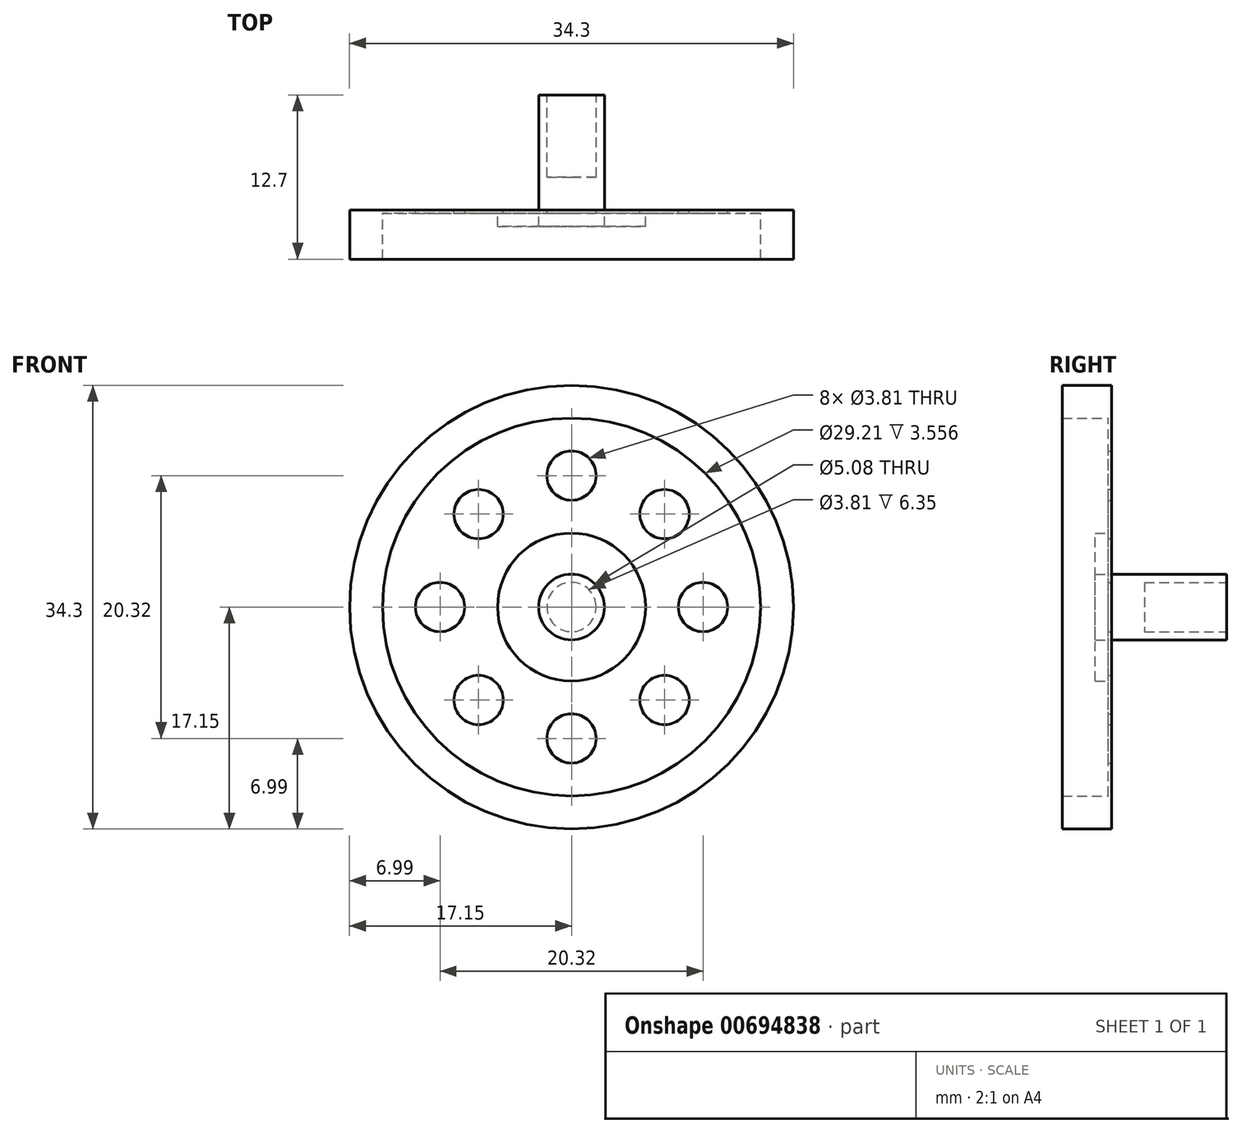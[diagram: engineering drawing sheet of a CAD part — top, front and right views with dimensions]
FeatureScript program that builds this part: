
annotation { "Feature Type Name" : "Feature", "Feature Type Description" : "" }
export const myFeature = defineFeature(function(context is Context, id is Id, definition is map)
    precondition{}
    {
        {
            var Q0;
            Q0=qCreatedBy(makeId("Front.planeOp"),FACE);
            var sketch = newSketch(context, id + "F0", { "sketchPlane" : qUnion([Q0])});
            skCircle(sketch, "E0", {"center": v(0, 0) * mm, "radius": 17.15 * mm});
            skCircle(sketch, "E1.0", {"center": v(0, 0) * mm, "radius": 14.6 * mm});
            skCircle(sketch, "E2", {"center": v(0, 0) * mm, "radius": 2.54 * mm});
            skCircle(sketch, "E3", {"center": v(0, 0) * mm, "radius": 5.72 * mm});
            skCircle(sketch, "E4", {"center": v(0, 10.16) * mm, "radius": 1.9 * mm});
            skCircle(sketch, "E5.1.0", {"center": v(-7.18, 7.18) * mm, "radius": 1.9 * mm});
            skCircle(sketch, "E5.2.0", {"center": v(-10.16, 0) * mm, "radius": 1.9 * mm});
            skCircle(sketch, "E5.3.0", {"center": v(-7.18, -7.18) * mm, "radius": 1.9 * mm});
            skCircle(sketch, "E5.4.0", {"center": v(0, -10.16) * mm, "radius": 1.9 * mm});
            skCircle(sketch, "E5.5.0", {"center": v(7.18, -7.18) * mm, "radius": 1.9 * mm});
            skCircle(sketch, "E5.6.0", {"center": v(10.16, 0) * mm, "radius": 1.9 * mm});
            skCircle(sketch, "E5.7.0", {"center": v(7.18, 7.18) * mm, "radius": 1.9 * mm});
            skSolve(sketch);
        }
        {
            var Q0;
            Q0=makeQuery(id+"F0.imprint","IMPRINT",FACE,{"disambiguationData":[TD([[makeQuery(id+"F0.imprint","IMPRINT",EDGE,{"derivedFrom":sQuery(id+"F0.wireOp",EDGE,"E0")}),1.0]])]});
            extrude(context, id + "F1", {"entities" : qUnion([Q0]), "depth" : 3.8 * mm, "offsetDistance" : 25.4 * mm});
        }
        {
            var Q0;
            Q0=makeQuery(id+"F0.imprint","IMPRINT",FACE,{"disambiguationData":[TD([[makeQuery(id+"F0.imprint","IMPRINT",EDGE,{"derivedFrom":sQuery(id+"F0.wireOp",EDGE,"E2")}),-1.0]])]});
            extrude(context, id + "F2", {"entities" : qUnion([Q0]), "operationType" : NewBodyOperationType.ADD, "depth" : 1.27 * mm, "offsetDistance" : 25.4 * mm});
        }
        {
            var Q0;
            Q0=makeQuery(id+"F0.imprint","IMPRINT",FACE,{"disambiguationData":[TD([[makeQuery(id+"F0.imprint","IMPRINT",EDGE,{"derivedFrom":sQuery(id+"F0.wireOp",EDGE,"E3")}),-1.0]])]});
            extrude(context, id + "F3", {"entities" : qUnion([Q0]), "operationType" : NewBodyOperationType.ADD, "depth" : 0.25 * mm, "offsetDistance" : 25.4 * mm});
        }
        {
            var Q0;
            Q0=makeQuery(id+"F0.imprint","IMPRINT",FACE,{"disambiguationData":[TD([[makeQuery(id+"F0.imprint","IMPRINT",EDGE,{"derivedFrom":sQuery(id+"F0.wireOp",EDGE,"E2")}),1.0]])]});
            extrude(context, id + "F4", {"entities" : qUnion([Q0]), "operationType" : NewBodyOperationType.ADD, "oppositeDirection" : true, "depth" : 8.9 * mm, "offsetDistance" : 25.4 * mm});
        }
        {
            var Q0;
            Q0=makeQuery(id+"F4.opExtrude","CAP_FACE",FACE,{"disambiguationData":[OSD([sQuery(id+"F0.wireOp",EDGE,"E2")])],"isStart":false});
            var sketch = newSketch(context, id + "F5", { "sketchPlane" : qUnion([Q0])});
            skCircle(sketch, "E6", {"center": v(0, 0) * mm, "radius": 1.9 * mm});
            skSolve(sketch);
        }
        {
            var Q0;
            Q0=makeQuery(id+"F5.imprint","IMPRINT",FACE,{"disambiguationData":[TD([[makeQuery(id+"F5.imprint","IMPRINT",EDGE,{"derivedFrom":sQuery(id+"F5.wireOp",EDGE,"E6")}),1.0]])]});
            extrude(context, id + "F6", {"entities" : qUnion([Q0]), "operationType" : NewBodyOperationType.REMOVE, "oppositeDirection" : true, "depth" : 6.35 * mm, "offsetDistance" : 25.4 * mm});
        }
    });
